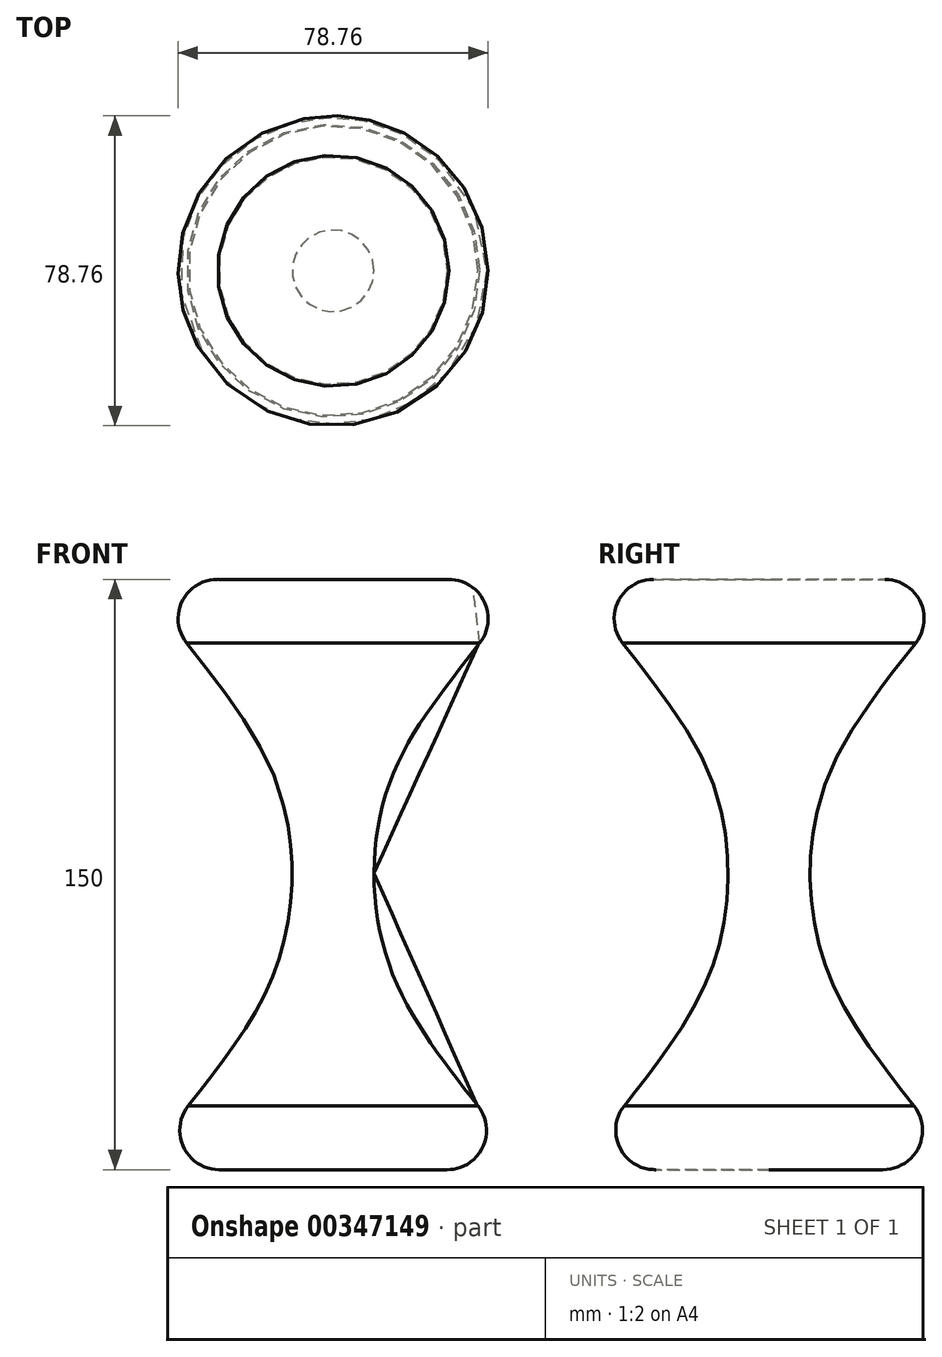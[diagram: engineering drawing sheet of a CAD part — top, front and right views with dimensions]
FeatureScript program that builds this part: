
annotation { "Feature Type Name" : "Feature", "Feature Type Description" : "" }
export const myFeature = defineFeature(function(context is Context, id is Id, definition is map)
    precondition{}
    {
        {
            var Q0;
            Q0=qCreatedBy(makeId("Top.planeOp"),FACE);
            var sketch = newSketch(context, id + "F0", { "sketchPlane" : qUnion([Q0])});
            skCircle(sketch, "E0", {"center": v(0, 0) * mm, "radius": 50 * mm});
            skSolve(sketch);
        }
        {
            var Q0;
            Q0=qCreatedBy(makeId("Top.planeOp"),FACE);
            cPlane(context, id + "F1", {"entities" : qUnion([Q0]), "cplaneType" : CPlaneType.OFFSET, "offset" : 25 * mm, "width" : 150 * mm, "height" : 150 * mm});
        }
        {
            var Q0;
            Q0=qCreatedBy(id+"F1.planeOp",FACE);
            var sketch = newSketch(context, id + "F2", { "sketchPlane" : qUnion([Q0])});
            skCircle(sketch, "E1", {"center": v(0, 0) * mm, "radius": 30 * mm});
            skSolve(sketch);
        }
        {
            var Q0;
            Q0=qCreatedBy(id+"F1.planeOp",FACE);
            cPlane(context, id + "F3", {"entities" : qUnion([Q0]), "cplaneType" : CPlaneType.OFFSET, "offset" : 25 * mm, "width" : 150 * mm, "height" : 150 * mm});
        }
        {
            var Q0;
            Q0=qCreatedBy(id+"F3.planeOp",FACE);
            var sketch = newSketch(context, id + "F4", { "sketchPlane" : qUnion([Q0])});
            skCircle(sketch, "E2", {"center": v(0, 0) * mm, "radius": 15 * mm});
            skSolve(sketch);
        }
        {
            var Q0;
            Q0=qCreatedBy(id+"F3.planeOp",FACE);
            cPlane(context, id + "F5", {"entities" : qUnion([Q0]), "cplaneType" : CPlaneType.OFFSET, "offset" : 25 * mm, "width" : 150 * mm, "height" : 150 * mm});
        }
        {
            var Q0;
            Q0=qCreatedBy(id+"F5.planeOp",FACE);
            cPlane(context, id + "F6", {"entities" : qUnion([Q0]), "cplaneType" : CPlaneType.OFFSET, "offset" : 25 * mm, "width" : 150 * mm, "height" : 150 * mm});
        }
        {
            var Q0;
            Q0=qCreatedBy(id+"F6.planeOp",FACE);
            var sketch = newSketch(context, id + "F7", { "sketchPlane" : qUnion([Q0])});
            skCircle(sketch, "E3", {"center": v(0, 0) * mm, "radius": 15 * mm});
            skSolve(sketch);
        }
        {
            var Q0;
            Q0=qCreatedBy(id+"F6.planeOp",FACE);
            cPlane(context, id + "F8", {"entities" : qUnion([Q0]), "cplaneType" : CPlaneType.OFFSET, "offset" : 25 * mm, "width" : 150 * mm, "height" : 150 * mm});
        }
        {
            var Q0;
            Q0=qCreatedBy(id+"F8.planeOp",FACE);
            var sketch = newSketch(context, id + "F9", { "sketchPlane" : qUnion([Q0])});
            skCircle(sketch, "E4", {"center": v(0, 0) * mm, "radius": 30.4 * mm});
            skSolve(sketch);
        }
        {
            var Q0;
            Q0=qCreatedBy(id+"F8.planeOp",FACE);
            cPlane(context, id + "F10", {"entities" : qUnion([Q0]), "cplaneType" : CPlaneType.OFFSET, "offset" : 25 * mm, "width" : 150 * mm, "height" : 150 * mm});
        }
        {
            var Q0;
            Q0=qCreatedBy(id+"F10.planeOp",FACE);
            var sketch = newSketch(context, id + "F11", { "sketchPlane" : qUnion([Q0])});
            skCircle(sketch, "E5", {"center": v(0, 0) * mm, "radius": 50.15 * mm});
            skSolve(sketch);
        }
        {
            var Q0;
            Q0=makeQuery(id+"F0.imprint","IMPRINT",FACE,{"disambiguationData":[TD([[makeQuery(id+"F0.imprint","IMPRINT",EDGE,{"derivedFrom":sQuery(id+"F0.wireOp",EDGE,"E0")}),1.0]])]});
            var Q1;
            Q1=makeQuery(id+"F2.imprint","IMPRINT",FACE,{"disambiguationData":[TD([[makeQuery(id+"F2.imprint","IMPRINT",EDGE,{"derivedFrom":sQuery(id+"F2.wireOp",EDGE,"E1")}),1.0]])]});
            var Q2;
            Q2=makeQuery(id+"F4.imprint","IMPRINT",FACE,{"disambiguationData":[TD([[makeQuery(id+"F4.imprint","IMPRINT",EDGE,{"derivedFrom":sQuery(id+"F4.wireOp",EDGE,"E2")}),1.0]])]});
            var Q3;
            Q3=makeQuery(id+"F7.imprint","IMPRINT",FACE,{"disambiguationData":[TD([[makeQuery(id+"F7.imprint","IMPRINT",EDGE,{"derivedFrom":sQuery(id+"F7.wireOp",EDGE,"E3")}),1.0]])]});
            var Q4;
            Q4=makeQuery(id+"F9.imprint","IMPRINT",FACE,{"disambiguationData":[TD([[makeQuery(id+"F9.imprint","IMPRINT",EDGE,{"derivedFrom":sQuery(id+"F9.wireOp",EDGE,"E4")}),1.0]])]});
            var Q5;
            Q5=makeQuery(id+"F11.imprint","IMPRINT",FACE,{"disambiguationData":[TD([[makeQuery(id+"F11.imprint","IMPRINT",EDGE,{"derivedFrom":sQuery(id+"F11.wireOp",EDGE,"E5")}),1.0]])]});
            loft(context, id + "F12", {"sheetProfilesArray" : [{ "sheetProfileEntities" : qUnion([Q0]) }, { "sheetProfileEntities" : qUnion([Q1]) }, { "sheetProfileEntities" : qUnion([Q2]) }, { "sheetProfileEntities" : qUnion([Q3]) }, { "sheetProfileEntities" : qUnion([Q4]) }, { "sheetProfileEntities" : qUnion([Q5]) }]});
        }
        {
            var Q0;
            Q0=makeQuery(id+"F12.opLoft","MID_CAP_EDGE",EDGE,{"disambiguationData":[OSD([sQuery(id+"F0.wireOp",EDGE,"E0"),sQuery(id+"F11.wireOp",EDGE,"E5")])],"capPos":5.0});
            fillet(context, id + "F13", {"entities" : qUnion([Q0]), "radius" : 10 * mm, "tangentPropagation" : true, "allowEdgeOverflow" : false});
        }
        {
            var Q0;
            Q0=makeQuery(id+"F12.opLoft","MID_CAP_EDGE",EDGE,{"disambiguationData":[OSD([sQuery(id+"F0.wireOp",EDGE,"E0")])],"capPos":0.0});
            fillet(context, id + "F14", {"entities" : qUnion([Q0]), "radius" : 10 * mm, "tangentPropagation" : true, "allowEdgeOverflow" : false});
        }
    });
